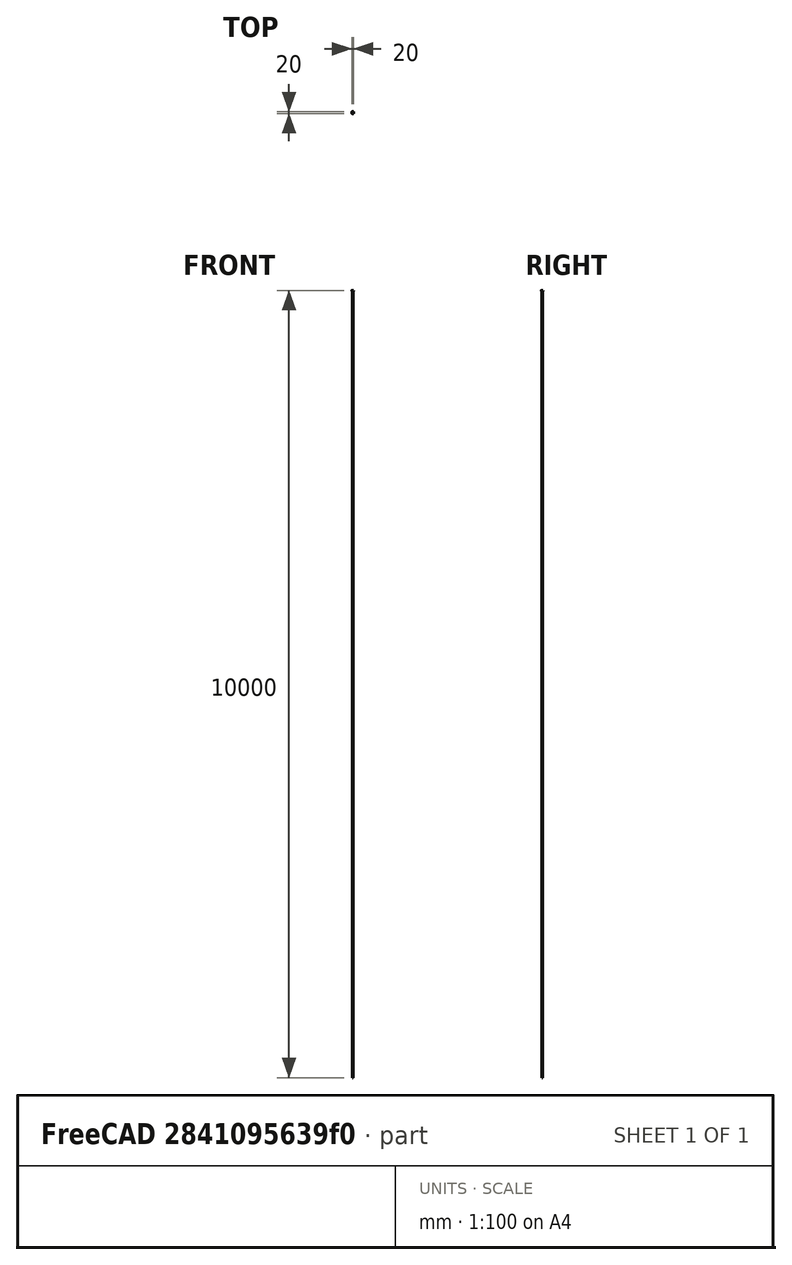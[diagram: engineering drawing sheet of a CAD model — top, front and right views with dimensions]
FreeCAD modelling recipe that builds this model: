
FCSTD DOCUMENT  (FreeCAD 0.14R3703 (Git))
Label: 20X20TIPUSB5MM
License: CC-BY 3.0
LicenseURL: http://creativecommons.org/licenses/by/3.0/
objects: Sketcher::SketchObject×2, PartDesign::Pad×1, PartDesign::Pocket×1
note: 6 computed .brp shape members not serialized (recipe doc carries the construction recipe); baked Part::Feature solids carry a one-line shape summary decoded from their .brp

FEATURE [Sketcher::SketchObject] Sketch
  Placement = pos=(1.5,0,0) rot=(0,0,1;0rad)
  sketch-geometry (136):
    g0: LineSegment StartX=0 StartY=20 StartZ=0 EndX=4.65 EndY=20 EndZ=0
    g1: ArcOfCircle CenterX=-1e-12 CenterY=18.5 CenterZ=0 NormalX=0 NormalY=0 NormalZ=1 Radius=1.5 StartAngle=1.5708 EndAngle=3.14159
    g2: LineSegment StartX=-1.5 StartY=13.85 StartZ=0 EndX=-1.5 EndY=18.5 EndZ=0
    g3: ArcOfCircle CenterX=-1.3 CenterY=13.85 CenterZ=0 NormalX=0 NormalY=0 NormalZ=1 Radius=0.2 StartAngle=3.14159 EndAngle=4.71239
    g4: LineSegment StartX=-1 StartY=13.65 StartZ=0 EndX=-1.3 EndY=13.65 EndZ=0
    g5: LineSegment StartX=-1 StartY=13.3 StartZ=0 EndX=-1 EndY=13.65 EndZ=0
    g6: ArcOfCircle CenterX=-0.8 CenterY=13.3 CenterZ=0 NormalX=0 NormalY=0 NormalZ=1 Radius=0.2 StartAngle=3.14159 EndAngle=4.71239
    g7: LineSegment StartX=-0.5 StartY=13.1 StartZ=0 EndX=-0.8 EndY=13.1 EndZ=0
    g8: ArcOfCircle CenterX=-0.5 CenterY=13.6 CenterZ=0 NormalX=0 NormalY=0 NormalZ=1 Radius=0.5 StartAngle=4.71239 EndAngle=6.28319
    g9: LineSegment StartX=2.68e-07 StartY=15.5 StartZ=0 EndX=2.68e-07 EndY=13.6 EndZ=0
    g10: ArcOfCircle CenterX=0.5 CenterY=15.5 CenterZ=0 NormalX=0 NormalY=0 NormalZ=1 Radius=0.5 StartAngle=1.5708 EndAngle=3.14159
    g11: LineSegment StartX=1.23223 StartY=16 StartZ=0 EndX=0.5 EndY=16 EndZ=0
    g12: ArcOfCircle CenterX=1.23223 CenterY=15.5 CenterZ=0 NormalX=0 NormalY=0 NormalZ=1 Radius=0.5 StartAngle=0.785398 EndAngle=1.5708
    g13: LineSegment StartX=3.85355 StartY=13.5858 StartZ=0 EndX=1.58579 EndY=15.8536 EndZ=0
    g14: ArcOfCircle CenterX=3.5 CenterY=13.2322 CenterZ=0 NormalX=0 NormalY=0 NormalZ=1 Radius=0.5 StartAngle=0 EndAngle=0.785398
    g15: LineSegment StartX=4 StartY=10.9536 StartZ=0 EndX=4 EndY=13.2322 EndZ=0
    g16: ArcOfCircle CenterX=4.2 CenterY=10.9536 CenterZ=0 NormalX=0 NormalY=0 NormalZ=1 Radius=0.2 StartAngle=3.14159 EndAngle=3.66519
    g17: LineSegment StartX=4.46188 StartY=10.1 StartZ=0 EndX=4.0268 EndY=10.8536 EndZ=0
    g18: ArcOfCircle CenterX=4.28868 CenterY=10 CenterZ=0 NormalX=0 NormalY=0 NormalZ=1 Radius=0.2 StartAngle=5.75959 EndAngle=6.80678
    g19: LineSegment StartX=4.0268 StartY=9.14641 StartZ=0 EndX=4.46188 EndY=9.9 EndZ=0
    g20: ArcOfCircle CenterX=4.2 CenterY=9.04641 CenterZ=0 NormalX=0 NormalY=0 NormalZ=1 Radius=0.2 StartAngle=2.61799 EndAngle=3.14159
    g21: LineSegment StartX=4 StartY=6.76777 StartZ=0 EndX=4 EndY=9.04641 EndZ=0
    g22: ArcOfCircle CenterX=3.5 CenterY=6.76777 CenterZ=0 NormalX=0 NormalY=0 NormalZ=1 Radius=0.5 StartAngle=5.49779 EndAngle=6.28319
    g23: LineSegment StartX=1.58579 StartY=4.14645 StartZ=0 EndX=3.85355 EndY=6.41421 EndZ=0
    g24: ArcOfCircle CenterX=1.23223 CenterY=4.5 CenterZ=0 NormalX=0 NormalY=0 NormalZ=1 Radius=0.5 StartAngle=4.71239 EndAngle=5.49779
    g25: LineSegment StartX=0.5 StartY=4 StartZ=0 EndX=1.23223 EndY=4 EndZ=0
    g26: ArcOfCircle CenterX=0.5 CenterY=4.5 CenterZ=0 NormalX=0 NormalY=0 NormalZ=1 Radius=0.5 StartAngle=3.14159 EndAngle=4.71239
    g27: LineSegment StartX=2.68e-07 StartY=6.4 StartZ=0 EndX=2.68e-07 EndY=4.5 EndZ=0
    g28: ArcOfCircle CenterX=-0.5 CenterY=6.4 CenterZ=0 NormalX=0 NormalY=0 NormalZ=1 Radius=0.5 StartAngle=0 EndAngle=1.5708
    g29: LineSegment StartX=-0.8 StartY=6.9 StartZ=0 EndX=-0.5 EndY=6.9 EndZ=0
    g30: ArcOfCircle CenterX=-0.8 CenterY=6.7 CenterZ=0 NormalX=0 NormalY=0 NormalZ=1 Radius=0.2 StartAngle=1.5708 EndAngle=3.14159
    g31: LineSegment StartX=-1 StartY=6.35 StartZ=0 EndX=-1 EndY=6.7 EndZ=0
    g32: LineSegment StartX=-1.3 StartY=6.35 StartZ=0 EndX=-1 EndY=6.35 EndZ=0
    g33: ArcOfCircle CenterX=-1.3 CenterY=6.15 CenterZ=0 NormalX=0 NormalY=0 NormalZ=1 Radius=0.2 StartAngle=1.5708 EndAngle=3.14159
    g34: LineSegment StartX=-1.5 StartY=1.5 StartZ=0 EndX=-1.5 EndY=6.15 EndZ=0
    g35: ArcOfCircle CenterX=0 CenterY=1.5 CenterZ=0 NormalX=0 NormalY=0 NormalZ=1 Radius=1.5 StartAngle=3.14159 EndAngle=4.71239
    g36: LineSegment StartX=4.65 StartY=1e-12 StartZ=0 EndX=0 EndY=0 EndZ=0
    g37: ArcOfCircle CenterX=4.65 CenterY=0.2 CenterZ=0 NormalX=0 NormalY=0 NormalZ=1 Radius=0.2 StartAngle=4.71239 EndAngle=6.28319
    g38: LineSegment StartX=4.85 StartY=0.5 StartZ=0 EndX=4.85 EndY=0.2 EndZ=0
    g39: LineSegment StartX=5.2 StartY=0.5 StartZ=0 EndX=4.85 EndY=0.5 EndZ=0
    g40: ArcOfCircle CenterX=5.2 CenterY=0.7 CenterZ=0 NormalX=0 NormalY=0 NormalZ=1 Radius=0.2 StartAngle=4.71239 EndAngle=6.28319
    g41: LineSegment StartX=5.4 StartY=1 StartZ=0 EndX=5.4 EndY=0.7 EndZ=0
    g42: ArcOfCircle CenterX=4.9 CenterY=1 CenterZ=0 NormalX=0 NormalY=0 NormalZ=1 Radius=0.5 StartAngle=0 EndAngle=1.5708
    g43: LineSegment StartX=3 StartY=1.5 StartZ=0 EndX=4.9 EndY=1.5 EndZ=0
    g44: ArcOfCircle CenterX=3 CenterY=2 CenterZ=0 NormalX=0 NormalY=0 NormalZ=1 Radius=0.5 StartAngle=3.14159 EndAngle=4.71239
    g45: LineSegment StartX=2.5 StartY=2.73223 StartZ=0 EndX=2.5 EndY=2 EndZ=0
    g46: ArcOfCircle CenterX=3 CenterY=2.73223 CenterZ=0 NormalX=0 NormalY=0 NormalZ=1 Radius=0.5 StartAngle=2.35619 EndAngle=3.14159
    g47: LineSegment StartX=4.91421 StartY=5.35355 StartZ=0 EndX=2.64645 EndY=3.08579 EndZ=0
    g48: ArcOfCircle CenterX=5.26777 CenterY=5 CenterZ=0 NormalX=0 NormalY=0 NormalZ=1 Radius=0.5 StartAngle=1.5708 EndAngle=2.35619
    g49: LineSegment StartX=7.54641 StartY=5.5 StartZ=0 EndX=5.26777 EndY=5.5 EndZ=0
    g50: ArcOfCircle CenterX=7.54641 CenterY=5.7 CenterZ=0 NormalX=0 NormalY=0 NormalZ=1 Radius=0.2 StartAngle=4.71239 EndAngle=5.23599
    g51: LineSegment StartX=8.4 StartY=5.96188 StartZ=0 EndX=7.64641 EndY=5.52679 EndZ=0
    g52: ArcOfCircle CenterX=8.5 CenterY=5.78868 CenterZ=0 NormalX=0 NormalY=0 NormalZ=1 Radius=0.2 StartAngle=1.0472 EndAngle=2.0944
    g53: LineSegment StartX=9.35359 StartY=5.52679 StartZ=0 EndX=8.6 EndY=5.96188 EndZ=0
    g54: ArcOfCircle CenterX=9.45359 CenterY=5.7 CenterZ=0 NormalX=0 NormalY=0 NormalZ=1 Radius=0.2 StartAngle=4.18879 EndAngle=4.71239
    g55: LineSegment StartX=11.7322 StartY=5.5 StartZ=0 EndX=9.45359 EndY=5.5 EndZ=0
    g56: ArcOfCircle CenterX=11.7322 CenterY=5 CenterZ=0 NormalX=0 NormalY=0 NormalZ=1 Radius=0.5 StartAngle=0.785398 EndAngle=1.5708
    g57: LineSegment StartX=14.3536 StartY=3.08579 StartZ=0 EndX=12.0858 EndY=5.35355 EndZ=0
    g58: ArcOfCircle CenterX=14 CenterY=2.73223 CenterZ=0 NormalX=0 NormalY=0 NormalZ=1 Radius=0.5 StartAngle=0 EndAngle=0.785398
    g59: LineSegment StartX=14.5 StartY=2 StartZ=0 EndX=14.5 EndY=2.73223 EndZ=0
    g60: ArcOfCircle CenterX=14 CenterY=2 CenterZ=0 NormalX=0 NormalY=0 NormalZ=1 Radius=0.5 StartAngle=4.71239 EndAngle=6.28319
    g61: LineSegment StartX=12.1 StartY=1.5 StartZ=0 EndX=14 EndY=1.5 EndZ=0
    g62: ArcOfCircle CenterX=12.1 CenterY=1 CenterZ=0 NormalX=0 NormalY=0 NormalZ=1 Radius=0.5 StartAngle=1.5708 EndAngle=3.14159
    g63: LineSegment StartX=11.6 StartY=0.7 StartZ=0 EndX=11.6 EndY=1 EndZ=0
    g64: ArcOfCircle CenterX=11.8 CenterY=0.7 CenterZ=0 NormalX=0 NormalY=0 NormalZ=1 Radius=0.2 StartAngle=3.14159 EndAngle=4.71239
    g65: LineSegment StartX=12.15 StartY=0.5 StartZ=0 EndX=11.8 EndY=0.5 EndZ=0
    g66: LineSegment StartX=12.15 StartY=0.2 StartZ=0 EndX=12.15 EndY=0.5 EndZ=0
    g67: ArcOfCircle CenterX=12.35 CenterY=0.2 CenterZ=0 NormalX=0 NormalY=0 NormalZ=1 Radius=0.2 StartAngle=3.14159 EndAngle=4.71239
    g68: LineSegment StartX=17 StartY=1e-12 StartZ=0 EndX=12.35 EndY=0 EndZ=0
    g69: ArcOfCircle CenterX=17 CenterY=1.5 CenterZ=0 NormalX=0 NormalY=0 NormalZ=1 Radius=1.5 StartAngle=4.71239 EndAngle=6.28319
    g70: LineSegment StartX=18.5 StartY=6.15 StartZ=0 EndX=18.5 EndY=1.5 EndZ=0
    g71: ArcOfCircle CenterX=18.3 CenterY=6.15 CenterZ=0 NormalX=0 NormalY=0 NormalZ=1 Radius=0.2 StartAngle=0 EndAngle=1.5708
    g72: LineSegment StartX=18 StartY=6.35 StartZ=0 EndX=18.3 EndY=6.35 EndZ=0
    g73: LineSegment StartX=18 StartY=6.7 StartZ=0 EndX=18 EndY=6.35 EndZ=0
    g74: ArcOfCircle CenterX=17.8 CenterY=6.7 CenterZ=0 NormalX=0 NormalY=0 NormalZ=1 Radius=0.2 StartAngle=0 EndAngle=1.5708
    g75: LineSegment StartX=17.5 StartY=6.9 StartZ=0 EndX=17.8 EndY=6.9 EndZ=0
    g76: ArcOfCircle CenterX=17.5 CenterY=6.4 CenterZ=0 NormalX=0 NormalY=0 NormalZ=1 Radius=0.5 StartAngle=1.5708 EndAngle=3.14159
    g77: LineSegment StartX=17 StartY=4.5 StartZ=0 EndX=17 EndY=6.4 EndZ=0
    g78: ArcOfCircle CenterX=16.5 CenterY=4.5 CenterZ=0 NormalX=0 NormalY=0 NormalZ=1 Radius=0.5 StartAngle=4.71239 EndAngle=6.28319
    g79: LineSegment StartX=15.7678 StartY=4 StartZ=0 EndX=16.5 EndY=4 EndZ=0
    g80: ArcOfCircle CenterX=15.7678 CenterY=4.5 CenterZ=0 NormalX=0 NormalY=0 NormalZ=1 Radius=0.5 StartAngle=3.92699 EndAngle=4.71239
    g81: LineSegment StartX=13.1464 StartY=6.41421 StartZ=0 EndX=15.4142 EndY=4.14645 EndZ=0
    g82: ArcOfCircle CenterX=13.5 CenterY=6.76777 CenterZ=0 NormalX=0 NormalY=0 NormalZ=1 Radius=0.5 StartAngle=3.14159 EndAngle=3.92699
    g83: LineSegment StartX=13 StartY=9.04641 StartZ=0 EndX=13 EndY=6.76777 EndZ=0
    g84: ArcOfCircle CenterX=12.8 CenterY=9.04641 CenterZ=0 NormalX=0 NormalY=0 NormalZ=1 Radius=0.2 StartAngle=0 EndAngle=0.523599
    g85: LineSegment StartX=12.5381 StartY=9.9 StartZ=0 EndX=12.9732 EndY=9.14641 EndZ=0
    g86: ArcOfCircle CenterX=12.7113 CenterY=10 CenterZ=0 NormalX=0 NormalY=0 NormalZ=1 Radius=0.2 StartAngle=2.61799 EndAngle=3.66519
    g87: LineSegment StartX=12.9732 StartY=10.8536 StartZ=0 EndX=12.5381 EndY=10.1 EndZ=0
    g88: ArcOfCircle CenterX=12.8 CenterY=10.9536 CenterZ=0 NormalX=0 NormalY=0 NormalZ=1 Radius=0.2 StartAngle=5.75959 EndAngle=6.28319
    g89: LineSegment StartX=13 StartY=13.2322 StartZ=0 EndX=13 EndY=10.9536 EndZ=0
    g90: ArcOfCircle CenterX=13.5 CenterY=13.2322 CenterZ=0 NormalX=0 NormalY=0 NormalZ=1 Radius=0.5 StartAngle=2.35619 EndAngle=3.14159
    g91: LineSegment StartX=15.4142 StartY=15.8536 StartZ=0 EndX=13.1464 EndY=13.5858 EndZ=0
    g92: ArcOfCircle CenterX=15.7678 CenterY=15.5 CenterZ=0 NormalX=0 NormalY=0 NormalZ=1 Radius=0.5 StartAngle=1.5708 EndAngle=2.35619
    g93: LineSegment StartX=16.5 StartY=16 StartZ=0 EndX=15.7678 EndY=16 EndZ=0
    g94: ArcOfCircle CenterX=16.5 CenterY=15.5 CenterZ=0 NormalX=0 NormalY=0 NormalZ=1 Radius=0.5 StartAngle=0 EndAngle=1.5708
    g95: LineSegment StartX=17 StartY=13.6 StartZ=0 EndX=17 EndY=15.5 EndZ=0
    g96: ArcOfCircle CenterX=17.5 CenterY=13.6 CenterZ=0 NormalX=0 NormalY=0 NormalZ=1 Radius=0.5 StartAngle=3.14159 EndAngle=4.71239
    g97: LineSegment StartX=17.8 StartY=13.1 StartZ=0 EndX=17.5 EndY=13.1 EndZ=0
    g98: ArcOfCircle CenterX=17.8 CenterY=13.3 CenterZ=0 NormalX=0 NormalY=0 NormalZ=1 Radius=0.2 StartAngle=4.71239 EndAngle=6.28319
    g99: LineSegment StartX=18 StartY=13.65 StartZ=0 EndX=18 EndY=13.3 EndZ=0
    g100: LineSegment StartX=18.3 StartY=13.65 StartZ=0 EndX=18 EndY=13.65 EndZ=0
    g101: ArcOfCircle CenterX=18.3 CenterY=13.85 CenterZ=0 NormalX=0 NormalY=0 NormalZ=1 Radius=0.2 StartAngle=4.71239 EndAngle=6.28319
    g102: LineSegment StartX=18.5 StartY=18.5 StartZ=0 EndX=18.5 EndY=13.85 EndZ=0
    g103: ArcOfCircle CenterX=17 CenterY=18.5 CenterZ=0 NormalX=0 NormalY=0 NormalZ=1 Radius=1.5 StartAngle=0 EndAngle=1.5708
    g104: LineSegment StartX=12.35 StartY=20 StartZ=0 EndX=17 EndY=20 EndZ=0
    g105: ArcOfCircle CenterX=12.35 CenterY=19.8 CenterZ=0 NormalX=0 NormalY=0 NormalZ=1 Radius=0.2 StartAngle=1.5708 EndAngle=3.14159
    g106: LineSegment StartX=12.15 StartY=19.5 StartZ=0 EndX=12.15 EndY=19.8 EndZ=0
    g107: LineSegment StartX=11.8 StartY=19.5 StartZ=0 EndX=12.15 EndY=19.5 EndZ=0
    g108: ArcOfCircle CenterX=11.8 CenterY=19.3 CenterZ=0 NormalX=0 NormalY=0 NormalZ=1 Radius=0.2 StartAngle=1.5708 EndAngle=3.14159
    g109: LineSegment StartX=11.6 StartY=19 StartZ=0 EndX=11.6 EndY=19.3 EndZ=0
    g110: ArcOfCircle CenterX=12.1 CenterY=19 CenterZ=0 NormalX=0 NormalY=0 NormalZ=1 Radius=0.5 StartAngle=3.14159 EndAngle=4.71239
    g111: LineSegment StartX=14 StartY=18.5 StartZ=0 EndX=12.1 EndY=18.5 EndZ=0
    g112: ArcOfCircle CenterX=14 CenterY=18 CenterZ=0 NormalX=0 NormalY=0 NormalZ=1 Radius=0.5 StartAngle=0 EndAngle=1.5708
    g113: LineSegment StartX=14.5 StartY=17.2678 StartZ=0 EndX=14.5 EndY=18 EndZ=0
    g114: ArcOfCircle CenterX=14 CenterY=17.2678 CenterZ=0 NormalX=0 NormalY=0 NormalZ=1 Radius=0.5 StartAngle=5.49779 EndAngle=6.28319
    g115: LineSegment StartX=12.0858 StartY=14.6464 StartZ=0 EndX=14.3536 EndY=16.9142 EndZ=0
    g116: ArcOfCircle CenterX=11.7322 CenterY=15 CenterZ=0 NormalX=0 NormalY=0 NormalZ=1 Radius=0.5 StartAngle=4.71239 EndAngle=5.49779
    g117: LineSegment StartX=9.45359 StartY=14.5 StartZ=0 EndX=11.7322 EndY=14.5 EndZ=0
    g118: ArcOfCircle CenterX=9.45359 CenterY=14.3 CenterZ=0 NormalX=0 NormalY=0 NormalZ=1 Radius=0.2 StartAngle=1.5708 EndAngle=2.0944
    g119: LineSegment StartX=8.6 StartY=14.0381 StartZ=0 EndX=9.35359 EndY=14.4732 EndZ=0
    g120: ArcOfCircle CenterX=8.5 CenterY=14.2113 CenterZ=0 NormalX=0 NormalY=0 NormalZ=1 Radius=0.2 StartAngle=4.18879 EndAngle=5.23599
    g121: LineSegment StartX=7.64641 StartY=14.4732 StartZ=0 EndX=8.4 EndY=14.0381 EndZ=0
    g122: ArcOfCircle CenterX=7.54641 CenterY=14.3 CenterZ=0 NormalX=0 NormalY=0 NormalZ=1 Radius=0.2 StartAngle=1.0472 EndAngle=1.5708
    g123: LineSegment StartX=5.26777 StartY=14.5 StartZ=0 EndX=7.54641 EndY=14.5 EndZ=0
    g124: ArcOfCircle CenterX=5.26777 CenterY=15 CenterZ=0 NormalX=0 NormalY=0 NormalZ=1 Radius=0.5 StartAngle=3.92699 EndAngle=4.71239
    g125: LineSegment StartX=2.64645 StartY=16.9142 StartZ=0 EndX=4.91421 EndY=14.6464 EndZ=0
    g126: ArcOfCircle CenterX=3 CenterY=17.2678 CenterZ=0 NormalX=0 NormalY=0 NormalZ=1 Radius=0.5 StartAngle=3.14159 EndAngle=3.92699
    g127: LineSegment StartX=2.5 StartY=18 StartZ=0 EndX=2.5 EndY=17.2678 EndZ=0
    g128: ArcOfCircle CenterX=3 CenterY=18 CenterZ=0 NormalX=0 NormalY=0 NormalZ=1 Radius=0.5 StartAngle=1.5708 EndAngle=3.14159
    g129: LineSegment StartX=4.9 StartY=18.5 StartZ=0 EndX=3 EndY=18.5 EndZ=0
    g130: ArcOfCircle CenterX=4.9 CenterY=19 CenterZ=0 NormalX=0 NormalY=0 NormalZ=1 Radius=0.5 StartAngle=4.71239 EndAngle=6.28319
    g131: LineSegment StartX=5.4 StartY=19.3 StartZ=0 EndX=5.4 EndY=19 EndZ=0
    g132: ArcOfCircle CenterX=5.2 CenterY=19.3 CenterZ=0 NormalX=0 NormalY=0 NormalZ=1 Radius=0.2 StartAngle=0 EndAngle=1.5708
    g133: LineSegment StartX=4.85 StartY=19.5 StartZ=0 EndX=5.2 EndY=19.5 EndZ=0
    g134: LineSegment StartX=4.85 StartY=19.8 StartZ=0 EndX=4.85 EndY=19.5 EndZ=0
    g135: ArcOfCircle CenterX=4.65 CenterY=19.8 CenterZ=0 NormalX=0 NormalY=0 NormalZ=1 Radius=0.2 StartAngle=0 EndAngle=1.5708
  constraints (136):
    c: Coincident(g0,g1)
    c: Coincident(g135,g0)
    c: Coincident(g1,g2)
    c: Coincident(g2,g3)
    c: Coincident(g3,g4)
    c: Coincident(g4,g5)
    c: Coincident(g6,g5)
    c: Coincident(g7,g6)
    c: Coincident(g8,g7)
    c: Coincident(g9,g8)
    c: Coincident(g10,g9)
    c: Coincident(g10,g11)
    c: Coincident(g11,g12)
    c: Coincident(g12,g13)
    c: Coincident(g14,g13)
    c: Coincident(g15,g14)
    c: Coincident(g15,g16)
    c: Coincident(g16,g17)
    c: Coincident(g17,g18)
    c: Coincident(g18,g19)
    c: Coincident(g19,g20)
    c: Coincident(g20,g21)
    c: Coincident(g21,g22)
    c: Coincident(g22,g23)
    c: Coincident(g23,g24)
    c: Coincident(g24,g25)
    c: Coincident(g26,g25)
    c: Coincident(g26,g27)
    c: Coincident(g28,g27)
    c: Coincident(g28,g29)
    c: Coincident(g30,g29)
    c: Coincident(g31,g30)
    c: Coincident(g31,g32)
    c: Coincident(g32,g33)
    c: Coincident(g33,g34)
    c: Coincident(g35,g34)
    c: Coincident(g36,g35)
    c: Coincident(g37,g36)
    c: Coincident(g37,g38)
    c: Coincident(g38,g39)
    c: Coincident(g40,g39)
    c: Coincident(g40,g41)
    c: Coincident(g41,g42)
    c: Coincident(g43,g42)
    c: Coincident(g44,g43)
    c: Coincident(g44,g45)
    c: Coincident(g45,g46)
    c: Coincident(g46,g47)
    c: Coincident(g47,g48)
    c: Coincident(g49,g48)
    c: Coincident(g49,g50)
    c: Coincident(g50,g51)
    c: Coincident(g51,g52)
    c: Coincident(g53,g52)
    c: Coincident(g54,g53)
    c: Coincident(g55,g54)
    c: Coincident(g56,g55)
    c: Coincident(g56,g57)
    c: Coincident(g58,g57)
    c: Coincident(g59,g58)
    c: Coincident(g60,g59)
    c: Coincident(g61,g60)
    c: Coincident(g62,g61)
    c: Coincident(g62,g63)
    c: Coincident(g64,g63)
    c: Coincident(g65,g64)
    c: Coincident(g66,g65)
    c: Coincident(g67,g66)
    c: Coincident(g67,g68)
    c: Coincident(g69,g68)
    c: Coincident(g70,g69)
    c: Coincident(g71,g70)
    c: Coincident(g72,g71)
    c: Coincident(g73,g72)
    c: Coincident(g73,g74)
    c: Coincident(g75,g74)
    c: Coincident(g76,g75)
    c: Coincident(g76,g77)
    c: Coincident(g77,g78)
    c: Coincident(g78,g79)
    c: Coincident(g80,g79)
    c: Coincident(g81,g80)
    c: Coincident(g81,g82)
    c: Coincident(g82,g83)
    c: Coincident(g83,g84)
    c: Coincident(g85,g84)
    c: Coincident(g86,g85)
    c: Coincident(g86,g87)
    c: Coincident(g88,g87)
    c: Coincident(g88,g89)
    c: Coincident(g89,g90)
    c: Coincident(g91,g90)
    c: Coincident(g92,g91)
    c: Coincident(g93,g92)
    c: Coincident(g94,g93)
    c: Coincident(g94,g95)
    c: Coincident(g95,g96)
    c: Coincident(g96,g97)
    c: Coincident(g98,g97)
    c: Coincident(g98,g99)
    c: Coincident(g100,g99)
    c: Coincident(g100,g101)
    c: Coincident(g101,g102)
    c: Coincident(g102,g103)
    c: Coincident(g103,g104)
    c: Coincident(g104,g105)
    c: Coincident(g106,g105)
    c: Coincident(g107,g106)
    c: Coincident(g108,g107)
    c: Coincident(g109,g108)
    c: Coincident(g110,g109)
    c: Coincident(g111,g110)
    c: Coincident(g112,g111)
    c: Coincident(g112,g113)
    c: Coincident(g113,g114)
    c: Coincident(g114,g115)
    c: Coincident(g115,g116)
    c: Coincident(g117,g116)
    c: Coincident(g118,g117)
    c: Coincident(g119,g118)
    c: Coincident(g119,g120)
    c: Coincident(g121,g120)
    c: Coincident(g121,g122)
    c: Coincident(g122,g123)
    c: Coincident(g124,g123)
    c: Coincident(g124,g125)
    c: Coincident(g126,g125)
    c: Coincident(g127,g126)
    c: Coincident(g128,g127)
    c: Coincident(g129,g128)
    c: Coincident(g130,g129)
    c: Coincident(g130,g131)
    c: Coincident(g131,g132)
    c: Coincident(g133,g132)
    c: Coincident(g134,g133)
    c: Coincident(g135,g134)
FEATURE [PartDesign::Pad] Pad
  Length = 5
  Length2 = 100
  Placement = pos=(1.5,0,0) rot=(0,0,1;0rad)
  Sketch = -> Sketch
  Type = 0
FEATURE [Sketcher::SketchObject] Sketch001
  Placement = pos=(1.5,0,5) rot=(0,0,1;0rad)
  Support = -> Pad [Face138]
  sketch-geometry (16):
    g0: ArcOfCircle CenterX=8.5 CenterY=10 CenterZ=0 NormalX=0 NormalY=0 NormalZ=1 Radius=3.54978 StartAngle=2.14023 EndAngle=2.57348
    g1: LineSegment StartX=6.5861 StartY=12.9896 StartZ=0 EndX=7.24181 EndY=12.4453 EndZ=0
    g2: ArcOfCircle CenterX=8.5 CenterY=10 CenterZ=0 NormalX=0 NormalY=0 NormalZ=1 Radius=2.75 StartAngle=1.09559 EndAngle=2.046
    g3: LineSegment StartX=9.75819 StartY=12.4453 StartZ=0 EndX=10.4139 EndY=12.9896 EndZ=0
    g4: ArcOfCircle CenterX=8.5 CenterY=10 CenterZ=0 NormalX=0 NormalY=0 NormalZ=1 Radius=3.54978 StartAngle=0.568112 EndAngle=1.00136
    g5: LineSegment StartX=11.4922 StartY=11.9099 StartZ=0 EndX=10.9453 EndY=11.2582 EndZ=0
    g6: ArcOfCircle CenterX=8.5 CenterY=10 CenterZ=0 NormalX=0 NormalY=0 NormalZ=1 Radius=2.75 StartAngle=5.80798 EndAngle=6.75839
    g7: LineSegment StartX=10.9453 StartY=8.74181 StartZ=0 EndX=11.4922 EndY=8.09007 EndZ=0
    g8: ArcOfCircle CenterX=8.5 CenterY=10 CenterZ=0 NormalX=0 NormalY=0 NormalZ=1 Radius=3.54978 StartAngle=5.28183 EndAngle=5.71507
    g9: LineSegment StartX=10.4139 StartY=7.01036 StartZ=0 EndX=9.75819 EndY=7.5547 EndZ=0
    g10: ArcOfCircle CenterX=8.5 CenterY=10 CenterZ=0 NormalX=0 NormalY=0 NormalZ=1 Radius=2.75 StartAngle=4.23718 EndAngle=5.1876
    g11: LineSegment StartX=7.24181 StartY=7.5547 StartZ=0 EndX=6.5861 EndY=7.01036 EndZ=0
    g12: ArcOfCircle CenterX=8.5 CenterY=10 CenterZ=0 NormalX=0 NormalY=0 NormalZ=1 Radius=3.54978 StartAngle=3.7097 EndAngle=4.14295
    g13: LineSegment StartX=5.50783 StartY=8.09007 StartZ=0 EndX=6.0547 EndY=8.74181 EndZ=0
    g14: ArcOfCircle CenterX=8.5 CenterY=10 CenterZ=0 NormalX=0 NormalY=0 NormalZ=1 Radius=2.75 StartAngle=2.66639 EndAngle=3.6168
    g15: LineSegment StartX=6.0547 StartY=11.2582 StartZ=0 EndX=5.50783 EndY=11.9099 EndZ=0
  constraints (16):
    c: Coincident(g0,g1)
    c: Coincident(g15,g0)
    c: Coincident(g1,g2)
    c: Coincident(g3,g2)
    c: Coincident(g4,g3)
    c: Coincident(g4,g5)
    c: Coincident(g6,g5)
    c: Coincident(g7,g6)
    c: Coincident(g8,g7)
    c: Coincident(g9,g8)
    c: Coincident(g10,g9)
    c: Coincident(g11,g10)
    c: Coincident(g12,g11)
    c: Coincident(g13,g12)
    c: Coincident(g14,g13)
    c: Coincident(g15,g14)
FEATURE [PartDesign::Pocket] Pocket
  Length = 5
  Placement = pos=(1.5,0,0) rot=(0,0,1;0rad)
  Sketch = -> Sketch001
  Type = 1
